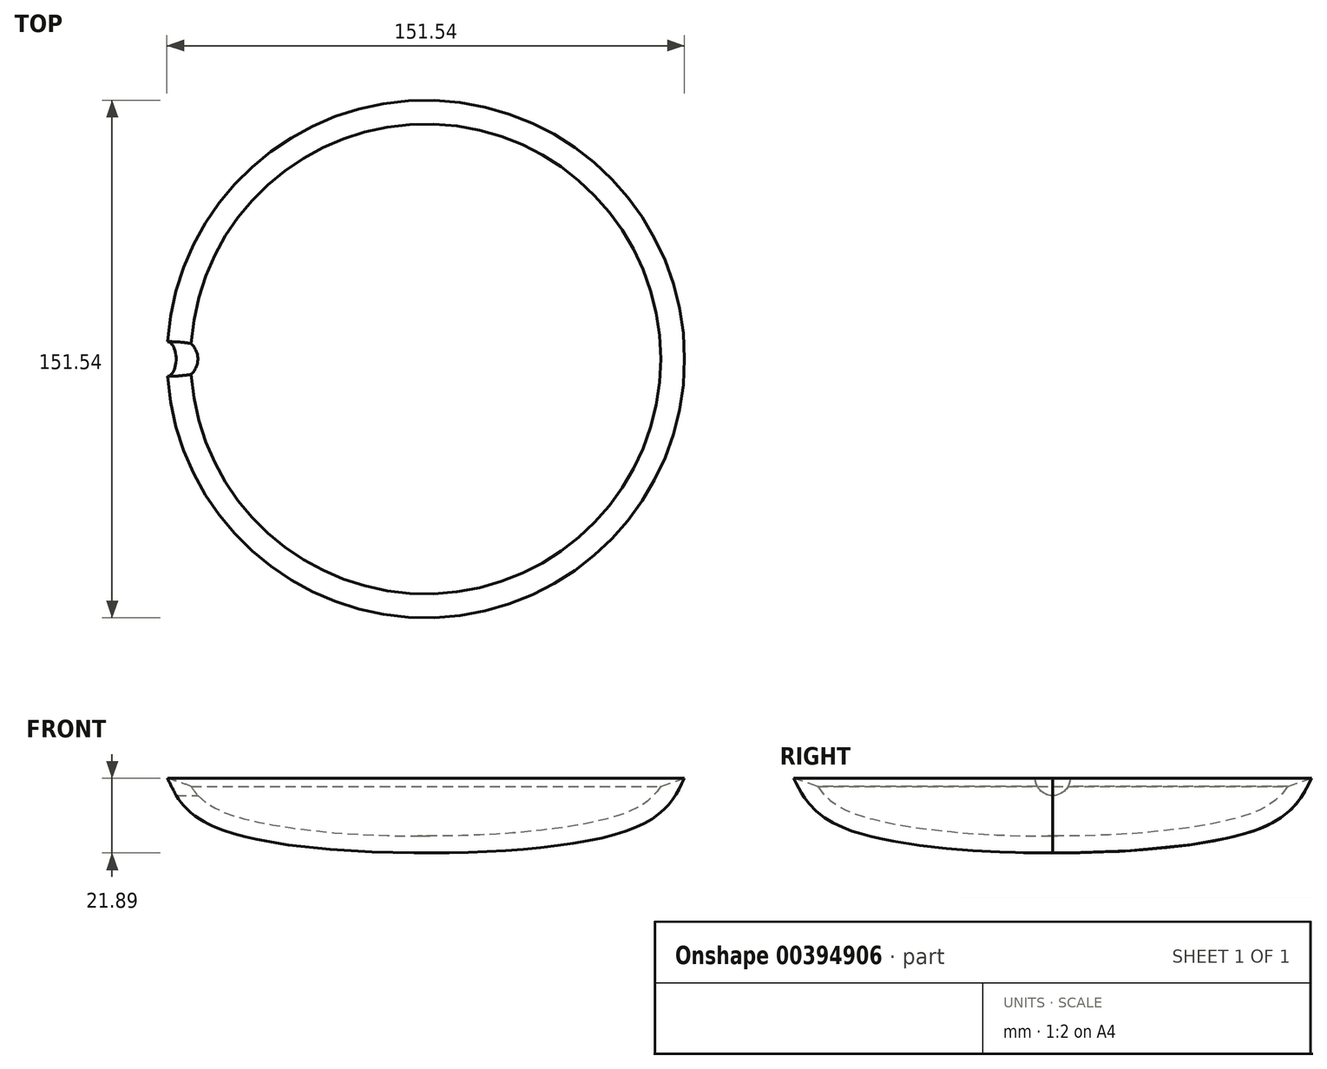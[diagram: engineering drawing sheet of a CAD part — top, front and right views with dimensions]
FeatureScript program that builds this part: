
annotation { "Feature Type Name" : "Feature", "Feature Type Description" : "" }
export const myFeature = defineFeature(function(context is Context, id is Id, definition is map)
    precondition{}
    {
        {
            var Q0;
            Q0=qCreatedBy(makeId("Front.planeOp"),FACE);
            var sketch = newSketch(context, id + "F0", { "sketchPlane" : qUnion([Q0])});
            skFitSpline(sketch, "E0", {"points": [v(75.77, 0) * mm, v(59.4, -15.23) * mm, v(-58.19, -15.23) * mm, v(-76.07, 0) * mm], "startDerivative": vector(-35.95, -73.3) * mm, "endDerivative": vector(-40.47, 71.4) * mm});
            skFitSpline(sketch, "E1.0", {"points": [v(71.2, 2.24) * mm, v(70.83, 1.47) * mm, v(70.12, 0.02) * mm, v(69.04, -1.94) * mm, v(67.86, -3.7) * mm, v(66.47, -5.32) * mm, v(64.7, -6.87) * mm, v(62.78, -8.14) * mm, v(60.87, -9.14) * mm, v(59.23, -9.87) * mm, v(57.36, -10.58) * mm, v(55.24, -11.27) * mm, v(52.88, -11.94) * mm, v(49.45, -12.77) * mm, v(44.65, -13.72) * mm, v(38.23, -14.7) * mm, v(28.95, -15.75) * mm, v(16.27, -16.62) * mm, v(0.2, -16.93) * mm, v(-15.88, -16.52) * mm, v(-28.56, -15.58) * mm, v(-37.84, -14.47) * mm, v(-44.26, -13.47) * mm, v(-49.05, -12.5) * mm, v(-52.49, -11.65) * mm, v(-54.85, -10.99) * mm, v(-56.97, -10.3) * mm, v(-59.48, -9.34) * mm, v(-62.08, -8.1) * mm, v(-64.5, -6.55) * mm, v(-66.38, -4.99) * mm, v(-67.9, -3.35) * mm, v(-69.21, -1.6) * mm, v(-70.42, 0.34) * mm, v(-71.23, 1.76) * mm, v(-71.65, 2.5) * mm]});
            skLineSegment(sketch, "E2", {"start": v(0, -21.9) * mm, "end": v(0, -16.81) * mm});
            skLineSegment(sketch, "E3", {"start": v(0, -16.81) * mm, "end": v(0, -21.9) * mm});
            skLineSegment(sketch, "E4", {"start": v(75.77, 0) * mm, "end": v(68.74, -2.37) * mm});
            skSolve(sketch);
        }
        {
            var Q0;
            Q0=makeQuery(id+"F0.imprint","IMPRINT",FACE,{"disambiguationData":[TD([[makeQuery(id+"F0.imprint","IMPRINT",EDGE,{"derivedFrom":sQuery(id+"F0.wireOp",EDGE,"E0")}),-1.0]])]});
            var Q1;
            Q1=sQuery(id+"F0.wireOp",EDGE,"E3");
            revolve(context, id + "F1", {"entities" : qUnion([Q0]), "axis" : qUnion([Q1]), "revolveType" : RevolveType.FULL});
        }
        {
            var Q0;
            Q0=qCreatedBy(makeId("Right.planeOp"),FACE);
            var sketch = newSketch(context, id + "F2", { "sketchPlane" : qUnion([Q0])});
            skCircle(sketch, "E5", {"center": v(0, 0) * mm, "radius": 5.08 * mm});
            skSolve(sketch);
        }
        {
            var Q0;
            Q0=qSketchRegion(id+"F2",true);
            extrude(context, id + "F3", {"entities" : qUnion([Q0]), "operationType" : NewBodyOperationType.REMOVE, "oppositeDirection" : true, "depth" : 101.6 * mm});
        }
    });
